# Revit family: PROOX Single toilet roll holder EN
name_source: partatom
category: Furniture
revit_build: Autodesk Revit 2014 (Build: 20130308_1515(x64)
units: mm (PartAtom-declared; Revit-internal decimal feet)

## types (2) — shared parameters
BIM objects producer = www.BIMtelligent.eu
Manufacturer = PROOX Ltd.
Product data sheet = http://www.proox.com
URL = http://www.proox.com

## per-type parameters (varying)
| type | Cost | Description | EAN-No. | Material | Model | Specification |
| ONE dark passion | 85 $ | single toilet roll holder PROOX ONE dark passion made from aluminum black anodized | 9120050350229 | PROOX Aluminum, black anodised | DP-380 | Single toilet roll holder made out from glass pearl blasted and black anodised aluminum. Intended for wall mounting. For rolls with max. 105mm width and minimum 17mm tube diameter. Including concealed mounting system with anchors and stainless steel adapter screws. |
| ONE pure | 81 $ | single toilet roll holder PROOX ONE pure made from stainless steel | 9120050350106 | PROOX Stainless steel, brushed | PU-380 | Single toilet roll holder completely machined from full stainless steel. Intended for wall mounting. For rolls with max. 105mm width and minimum 17mm tube diameter. Including concealed mounting system with anchors and stainless steel adapter screws. |

note: column(s) folded — value = type name in every type: Type Comments

## geometry (parser evidence)
native form markers: Sweep x1
no freeform markers — native parametric forms only
